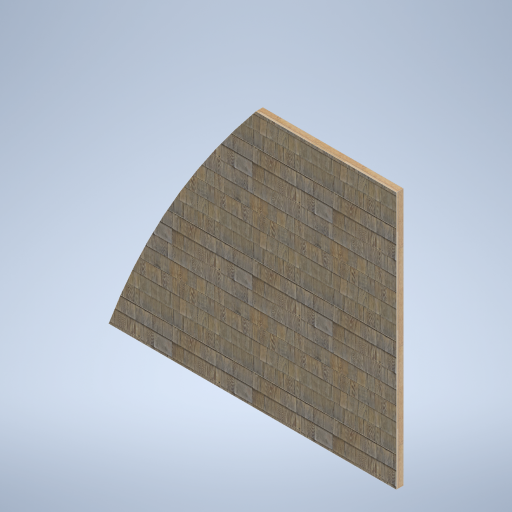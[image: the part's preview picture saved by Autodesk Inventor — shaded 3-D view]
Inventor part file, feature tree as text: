
AUTODESK INVENTOR PART (.ipt)
format: ipt  version: 2024.2 (Build 282272000, 272)  size: 402,944 bytes
history: native  units: mm
features: extrude x1, sketch x1
ambient origin geometry x8: Origin, YZ Plane, XZ Plane, XY Plane, X Axis, Y Axis, Z Axis, Center Point
bodies: Solid1 (feature_tree)
feature tree (2):
  extrude  "Extrusion1"  [1 undecoded]
  sketch  "Sketch1"  dims[d0=80.0mm d1=0.0mm]
note: 1 required parameter value undecoded (feature->parameter linkage not recoverable at this tier; creation-order binding heuristic only, values carry confidence <= 0.55)
